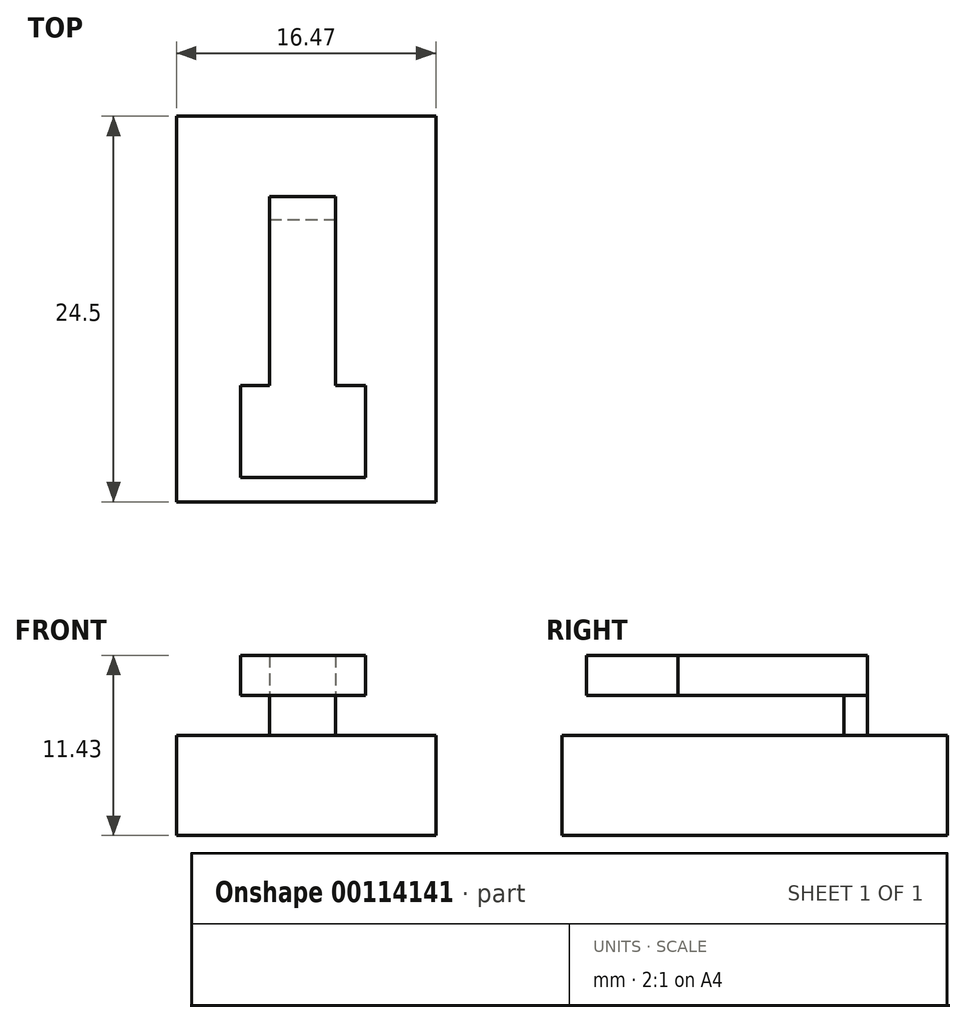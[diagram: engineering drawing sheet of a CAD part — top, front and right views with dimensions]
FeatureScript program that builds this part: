
annotation { "Feature Type Name" : "Feature", "Feature Type Description" : "" }
export const myFeature = defineFeature(function(context is Context, id is Id, definition is map)
    precondition{}
    {
        {
            var Q0;
            Q0=qCreatedBy(makeId("Top.planeOp"),FACE);
            var sketch = newSketch(context, id + "F0", { "sketchPlane" : qUnion([Q0])});
            skLineSegment(sketch, "E0.bottom", {"start": v(-7.99, 12.48) * mm, "end": v(8.48, 12.48) * mm});
            skLineSegment(sketch, "E0.top", {"start": v(-7.99, -12.02) * mm, "end": v(8.48, -12.02) * mm});
            skLineSegment(sketch, "E0.left", {"start": v(-7.99, 12.48) * mm, "end": v(-7.99, -12.02) * mm});
            skLineSegment(sketch, "E0.right", {"start": v(8.48, 12.48) * mm, "end": v(8.48, -12.02) * mm});
            skSolve(sketch);
        }
        {
            var Q0;
            Q0=makeQuery(id+"F0.imprint","IMPRINT",FACE,{"disambiguationData":[TD([[makeQuery(id+"F0.imprint","IMPRINT",EDGE,{"derivedFrom":sQuery(id+"F0.wireOp",EDGE,"E0.bottom")}),-1.0]])]});
            extrude(context, id + "F1", {"entities" : qUnion([Q0]), "depth" : 6.35 * mm});
        }
        {
            var Q0;
            Q0=makeQuery(id+"F1.opExtrude","CAP_FACE",FACE,{"disambiguationData":[OSD([sQuery(id+"F0.wireOp",EDGE,"E0.bottom"),sQuery(id+"F0.wireOp",EDGE,"E0.top"),sQuery(id+"F0.wireOp",EDGE,"E0.left"),sQuery(id+"F0.wireOp",EDGE,"E0.right")])],"isStart":false});
            var sketch = newSketch(context, id + "F2", { "sketchPlane" : qUnion([Q0])});
            skLineSegment(sketch, "E1.bottom", {"start": v(-7.99, 12.48) * mm, "end": v(8.48, 12.48) * mm});
            skLineSegment(sketch, "E1.top", {"start": v(-7.99, -12.02) * mm, "end": v(8.48, -12.02) * mm});
            skLineSegment(sketch, "E1.left", {"start": v(-7.99, 12.48) * mm, "end": v(-7.99, -12.02) * mm});
            skLineSegment(sketch, "E1.right", {"start": v(8.48, 12.48) * mm, "end": v(8.48, -12.02) * mm});
            skSolve(sketch);
        }
        {
            var Q0;
            Q0=makeQuery(id+"F2.imprint","IMPRINT",FACE,{"disambiguationData":[TD([[makeQuery(id+"F2.imprint","IMPRINT",EDGE,{"derivedFrom":sQuery(id+"F2.wireOp",EDGE,"E1.bottom")}),-1.0]])]});
            var sketch = newSketch(context, id + "F3", { "sketchPlane" : qUnion([Q0])});
            skLineSegment(sketch, "E2.bottom", {"start": v(-2.09, 7.38) * mm, "end": v(2.1, 7.38) * mm});
            skLineSegment(sketch, "E2.top", {"start": v(-2.09, 5.9) * mm, "end": v(2.1, 5.9) * mm});
            skLineSegment(sketch, "E2.left", {"start": v(-2.09, 7.38) * mm, "end": v(-2.09, 5.9) * mm});
            skLineSegment(sketch, "E2.right", {"start": v(2.1, 7.38) * mm, "end": v(2.1, 5.9) * mm});
            skSolve(sketch);
        }
        {
            var Q0;
            Q0=qSketchRegion(id+"F3",true);
            extrude(context, id + "F4", {"entities" : qUnion([Q0]), "depth" : 2.54 * mm});
        }
        {
            var Q0;
            Q0=makeQuery(id+"F4.opExtrude","CAP_FACE",FACE,{"disambiguationData":[OSD([sQuery(id+"F3.wireOp",EDGE,"E2.bottom"),sQuery(id+"F3.wireOp",EDGE,"E2.top"),sQuery(id+"F3.wireOp",EDGE,"E2.left"),sQuery(id+"F3.wireOp",EDGE,"E2.right")])],"isStart":false});
            var sketch = newSketch(context, id + "F5", { "sketchPlane" : qUnion([Q0])});
            skLineSegment(sketch, "E3.bottom", {"start": v(-2.09, 7.38) * mm, "end": v(2.1, 7.38) * mm});
            skLineSegment(sketch, "E3.top", {"start": v(-2.09, -10.45) * mm, "end": v(2.1, -10.45) * mm});
            skLineSegment(sketch, "E3.left", {"start": v(-2.09, 7.38) * mm, "end": v(-2.09, -10.45) * mm});
            skLineSegment(sketch, "E3.right", {"start": v(2.1, 7.38) * mm, "end": v(2.1, -10.45) * mm});
            skLineSegment(sketch, "E4.bottom", {"start": v(-3.92, -4.64) * mm, "end": v(4, -4.64) * mm});
            skLineSegment(sketch, "E4.top", {"start": v(-3.92, -10.47) * mm, "end": v(4, -10.47) * mm});
            skLineSegment(sketch, "E4.left", {"start": v(-3.92, -4.64) * mm, "end": v(-3.92, -10.47) * mm});
            skLineSegment(sketch, "E4.right", {"start": v(4, -4.64) * mm, "end": v(4, -10.47) * mm});
            skSolve(sketch);
        }
        {
            var Q0;
            Q0 = qSketchRegion(id + "F5", true);
            extrude(context, id + "F6", {"entities" : qUnion([Q0]), "depth" : 2.54 * mm});
        }
    });
